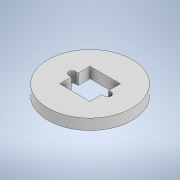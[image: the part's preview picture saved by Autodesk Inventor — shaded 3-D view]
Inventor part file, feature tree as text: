
AUTODESK INVENTOR PART (.ipt)
format: ipt  version: 2020 (Build 240168000, 168)  size: 146,944 bytes
history: native  units: mm
features: extrude x2, sketch x2, other x1, projected_geometry x1
ambient origin geometry x8: Origin, YZ Plane, XZ Plane, XY Plane, X Axis, Y Axis, Z Axis, Center Point
bodies: Body1 (feature_tree)
feature tree (6):
  other  "Твердое тело1"
  extrude  "Выдавливание1"  Depth=17.0mm
  extrude  "Выдавливание2"  Depth=17.0mm
  sketch  "Эскиз1"
  sketch  "Эскиз2"
  projected_geometry  "Спроецированная петля1"
